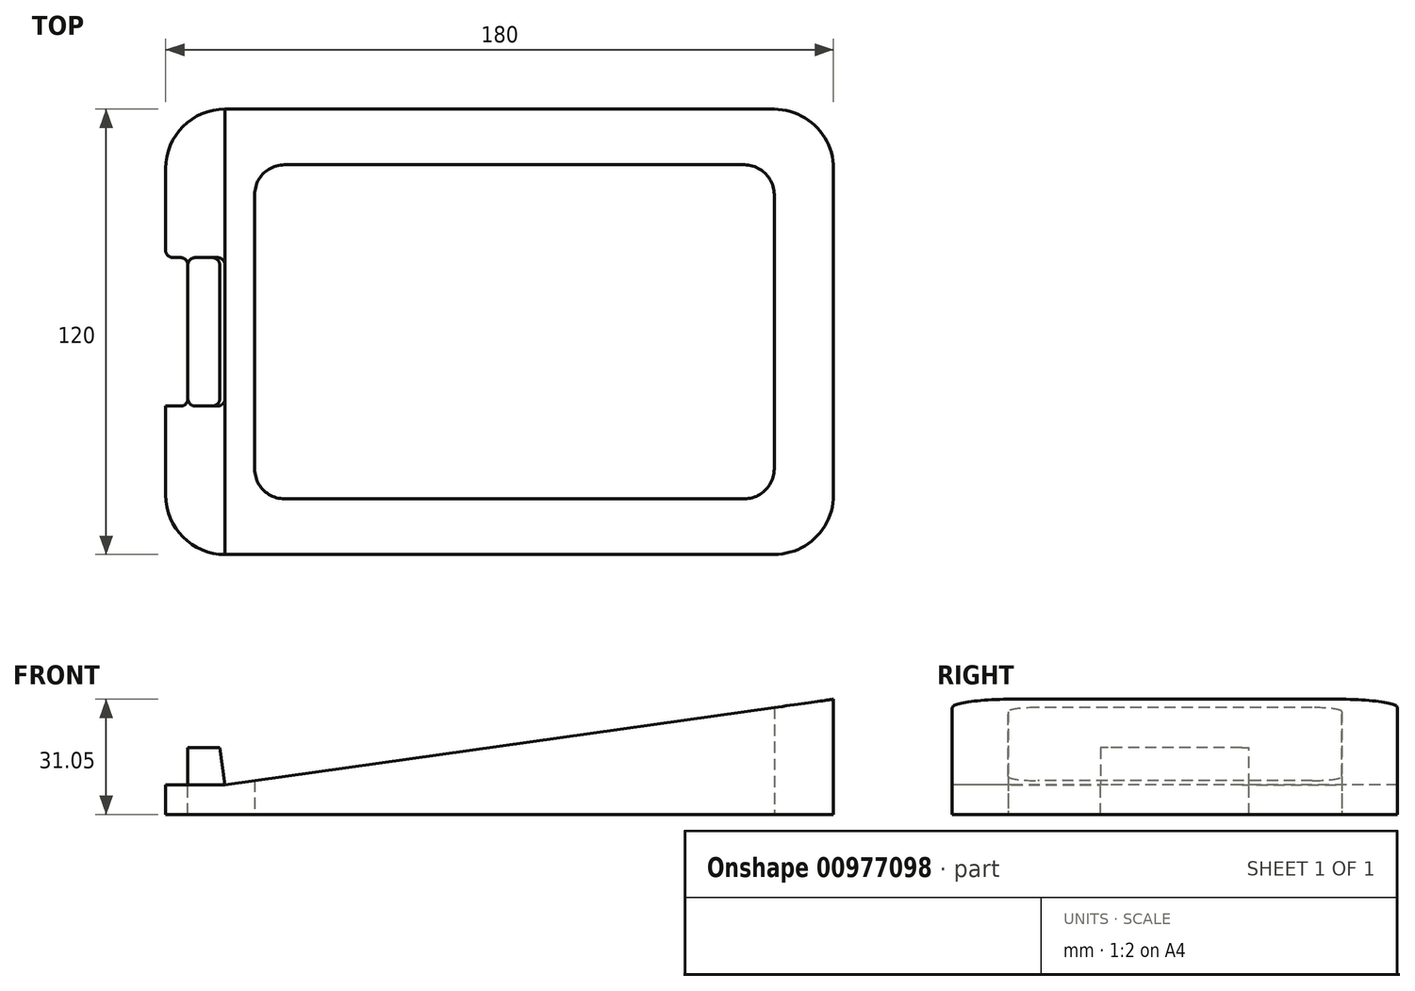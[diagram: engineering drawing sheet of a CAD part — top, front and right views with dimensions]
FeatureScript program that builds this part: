
annotation { "Feature Type Name" : "Feature", "Feature Type Description" : "" }
export const myFeature = defineFeature(function(context is Context, id is Id, definition is map)
    precondition{}
    {
        {
            assignVariable(context, id + "F0", {"name" : "Incline", "anyValue" : 8});
        }
        {
            var Q0;
            Q0=qCreatedBy(makeId("Top.planeOp"),FACE);
            var sketch = newSketch(context, id + "F1", { "sketchPlane" : qUnion([Q0])});
            skLineSegment(sketch, "E0.bottom", {"start": v(0, 0) * mm, "end": v(180, 0) * mm});
            skLineSegment(sketch, "E0.top", {"start": v(0, 120) * mm, "end": v(180, 120) * mm});
            skLineSegment(sketch, "E0.left", {"start": v(0, 0) * mm, "end": v(0, 120) * mm});
            skLineSegment(sketch, "E0.right", {"start": v(180, 0) * mm, "end": v(180, 120) * mm});
            skSolve(sketch);
        }
        {
            var Q0;
            Q0 = qSketchRegion(id + "F1", true);
            extrude(context, id + "F2", {"entities" : qUnion([Q0]), "depth" : 8 * mm, "offsetDistance" : 25 * mm});
        }
        {
            var Q0;
            Q0=makeQuery(id+"F2.opExtrude","SWEPT_FACE",FACE,{"disambiguationData":[OSD([sQuery(id+"F1.wireOp",EDGE,"E0.bottom")])]});
            var sketch = newSketch(context, id + "F3", { "sketchPlane" : qUnion([Q0])});
            skLineSegment(sketch, "E1", {"start": v(180, 8) * mm, "end": v(16, 8) * mm});
            skLineSegment(sketch, "E2", {"start": v(16, 8) * mm, "end": v(180, 31.05) * mm});
            skLineSegment(sketch, "E3", {"start": v(180, 31.05) * mm, "end": v(180, 8) * mm});
            skSolve(sketch);
        }
        {
            var Q0;
            Q0 = qSketchRegion(id + "F3", true);
            extrude(context, id + "F4", {"entities" : qUnion([Q0]), "operationType" : NewBodyOperationType.ADD, "oppositeDirection" : true, "depth" : 120 * mm, "offsetDistance" : 25 * mm});
        }
        {
            var Q0;
            Q0=makeQuery(id+"F2.opExtrude","CAP_FACE",FACE,{"disambiguationData":[OSD([sQuery(id+"F1.wireOp",EDGE,"E0.bottom"),sQuery(id+"F1.wireOp",EDGE,"E0.top"),sQuery(id+"F1.wireOp",EDGE,"E0.left"),sQuery(id+"F1.wireOp",EDGE,"E0.right")])],"isStart":false});
            var sketch = newSketch(context, id + "F5", { "sketchPlane" : qUnion([Q0])});
            skLineSegment(sketch, "E4.bottom", {"start": v(6, 80) * mm, "end": v(16, 80) * mm});
            skLineSegment(sketch, "E4.top", {"start": v(6, 40) * mm, "end": v(16, 40) * mm});
            skLineSegment(sketch, "E4.left", {"start": v(6, 80) * mm, "end": v(6, 40) * mm});
            skLineSegment(sketch, "E4.right", {"start": v(16, 80) * mm, "end": v(16, 40) * mm});
            skLineSegment(sketch, "E5", {"start": v(16, 60) * mm, "end": v(16, 60) * mm});
            skSolve(sketch);
        }
        {
            var Q0;
            Q0 = qSketchRegion(id + "F5", true);
            extrude(context, id + "F6", {"entities" : qUnion([Q0]), "operationType" : NewBodyOperationType.ADD, "depth" : 10 * mm, "offsetDistance" : 25 * mm});
        }
        {
            var Q0;
            Q0=makeQuery(id+"F6.opExtrude","CAP_EDGE",EDGE,{"disambiguationData":[OSD([sQuery(id+"F5.wireOp",EDGE,"E4.right")])],"isStart":false});
            chamfer(context, id + "F7", {"entities" : qUnion([Q0]), "chamferType" : ChamferType.OFFSET_ANGLE, "width" : 10 * mm, "oppositeDirection" : false, "angle" : (getVariable(context, 'Incline')) * degree, "tangentPropagation" : true});
        }
        {
            var Q0;
            Q0=makeQuery(id+"F2.opExtrude","CAP_FACE",FACE,{"disambiguationData":[OSD([sQuery(id+"F1.wireOp",EDGE,"E0.bottom"),sQuery(id+"F1.wireOp",EDGE,"E0.top"),sQuery(id+"F1.wireOp",EDGE,"E0.left"),sQuery(id+"F1.wireOp",EDGE,"E0.right")])],"isStart":true});
            var sketch = newSketch(context, id + "F8", { "sketchPlane" : qUnion([Q0])});
            skLineSegment(sketch, "E6.bottom", {"start": v(164, -15) * mm, "end": v(24, -15) * mm});
            skLineSegment(sketch, "E6.top", {"start": v(164, -105) * mm, "end": v(24, -105) * mm});
            skLineSegment(sketch, "E6.left", {"start": v(164, -15) * mm, "end": v(164, -105) * mm});
            skLineSegment(sketch, "E6.right", {"start": v(24, -15) * mm, "end": v(24, -105) * mm});
            skLineSegment(sketch, "E7", {"start": v(180, -60) * mm, "end": v(164, -60) * mm, "construction": true});
            skSolve(sketch);
        }
        {
            var Q0;
            Q0 = qSketchRegion(id + "F8", true);
            extrude(context, id + "F9", {"entities" : qUnion([Q0]), "operationType" : NewBodyOperationType.REMOVE, "endBound" : BoundingType.UP_TO_NEXT, "oppositeDirection" : true, "depth" : 25 * mm, "offsetDistance" : 25 * mm});
        }
        {
            var Q0;
            Q0=makeQuery(id+"F2.opExtrude","SWEPT_EDGE",EDGE,{"disambiguationData":[OSD([sQuery(id+"F1.wireOp",EDGE,"E0.bottom"),sQuery(id+"F1.wireOp",EDGE,"E0.left")])]});
            var Q1;
            Q1=makeQuery(id+"F2.opExtrude","SWEPT_EDGE",EDGE,{"disambiguationData":[OSD([sQuery(id+"F1.wireOp",EDGE,"E0.top"),sQuery(id+"F1.wireOp",EDGE,"E0.left")])]});
            var Q2;
            Q2=makeQuery(id+"F4.boolean.opBoolean","MERGE",EDGE,{"derivedFrom":[makeQuery(id+"F2.opExtrude","SWEPT_EDGE",EDGE,{"disambiguationData":[OSD([sQuery(id+"F1.wireOp",EDGE,"E0.top"),sQuery(id+"F1.wireOp",EDGE,"E0.right")])]}),makeQuery(id+"F4.opExtrude","CAP_EDGE",EDGE,{"disambiguationData":[OSD([sQuery(id+"F3.wireOp",EDGE,"E3")])],"isStart":false})]});
            var Q3;
            Q3=makeQuery(id+"F4.boolean.opBoolean","MERGE",EDGE,{"derivedFrom":[makeQuery(id+"F2.opExtrude","SWEPT_EDGE",EDGE,{"disambiguationData":[OSD([sQuery(id+"F1.wireOp",EDGE,"E0.bottom"),sQuery(id+"F1.wireOp",EDGE,"E0.right")])]}),makeQuery(id+"F4.opExtrude","CAP_EDGE",EDGE,{"disambiguationData":[OSD([sQuery(id+"F3.wireOp",EDGE,"E3")])],"isStart":true})]});
            fillet(context, id + "F10", {"entities" : qUnion([Q0, Q1, Q2, Q3]), "radius" : 16 * mm, "tangentPropagation" : true, "allowEdgeOverflow" : false});
        }
        {
            var Q0;
            Q0=makeQuery(id+"F9.boolean.opBoolean","COPY",EDGE,{"derivedFrom":makeQuery(id+"F9.opExtrude","SWEPT_EDGE",EDGE,{"disambiguationData":[OSD([sQuery(id+"F8.wireOp",EDGE,"E6.top"),sQuery(id+"F8.wireOp",EDGE,"E6.left")])]})});
            var Q1;
            Q1=makeQuery(id+"F9.boolean.opBoolean","COPY",EDGE,{"derivedFrom":makeQuery(id+"F9.opExtrude","SWEPT_EDGE",EDGE,{"disambiguationData":[OSD([sQuery(id+"F8.wireOp",EDGE,"E6.bottom"),sQuery(id+"F8.wireOp",EDGE,"E6.left")])]})});
            var Q2;
            Q2=makeQuery(id+"F9.boolean.opBoolean","COPY",EDGE,{"derivedFrom":makeQuery(id+"F9.opExtrude","SWEPT_EDGE",EDGE,{"disambiguationData":[OSD([sQuery(id+"F8.wireOp",EDGE,"E6.bottom"),sQuery(id+"F8.wireOp",EDGE,"E6.right")])]})});
            var Q3;
            Q3=makeQuery(id+"F9.boolean.opBoolean","COPY",EDGE,{"derivedFrom":makeQuery(id+"F9.opExtrude","SWEPT_EDGE",EDGE,{"disambiguationData":[OSD([sQuery(id+"F8.wireOp",EDGE,"E6.top"),sQuery(id+"F8.wireOp",EDGE,"E6.right")])]})});
            fillet(context, id + "F11", {"entities" : qUnion([Q0, Q1, Q2, Q3]), "radius" : 8 * mm, "tangentPropagation" : true, "allowEdgeOverflow" : false});
        }
        {
            var Q0;
            Q0=makeQuery(id+"F2.opExtrude","CAP_FACE",FACE,{"disambiguationData":[OSD([sQuery(id+"F1.wireOp",EDGE,"E0.bottom"),sQuery(id+"F1.wireOp",EDGE,"E0.top"),sQuery(id+"F1.wireOp",EDGE,"E0.left"),sQuery(id+"F1.wireOp",EDGE,"E0.right")])],"isStart":false});
            var sketch = newSketch(context, id + "F12", { "sketchPlane" : qUnion([Q0])});
            skLineSegment(sketch, "E8.bottom", {"start": v(6, 80) * mm, "end": v(0, 80) * mm});
            skLineSegment(sketch, "E8.top", {"start": v(6, 40) * mm, "end": v(0, 40) * mm});
            skLineSegment(sketch, "E8.left", {"start": v(6, 80) * mm, "end": v(6, 40) * mm});
            skLineSegment(sketch, "E8.right", {"start": v(0, 80) * mm, "end": v(0, 40) * mm});
            skSolve(sketch);
        }
        {
            var Q0;
            Q0 = qSketchRegion(id + "F12", true);
            extrude(context, id + "F13", {"entities" : qUnion([Q0]), "operationType" : NewBodyOperationType.REMOVE, "endBound" : BoundingType.UP_TO_NEXT, "oppositeDirection" : true, "depth" : 25 * mm, "offsetDistance" : 25 * mm});
        }
        {
            var Q0;
            Q0=makeQuery(id+"F13.boolean.opBoolean","COPY",EDGE,{"derivedFrom":makeQuery(id+"F13.opExtrude","SWEPT_EDGE",EDGE,{"disambiguationData":[OSD([sQuery(id+"F5.wireOp",EDGE,"E4.bottom"),sQuery(id+"F5.wireOp",EDGE,"E4.left"),sQuery(id+"F12.wireOp",EDGE,"E8.bottom"),sQuery(id+"F12.wireOp",EDGE,"E8.left")])]})});
            var Q1;
            Q1=makeQuery(id+"F13.boolean.opBoolean","COPY",EDGE,{"derivedFrom":makeQuery(id+"F13.opExtrude","SWEPT_EDGE",EDGE,{"disambiguationData":[OSD([sQuery(id+"F1.wireOp",EDGE,"E0.left"),sQuery(id+"F12.wireOp",EDGE,"E8.bottom"),sQuery(id+"F12.wireOp",EDGE,"E8.right")])]})});
            var Q2;
            Q2=makeQuery(id+"F13.boolean.opBoolean","COPY",EDGE,{"derivedFrom":makeQuery(id+"F13.opExtrude","SWEPT_EDGE",EDGE,{"disambiguationData":[OSD([sQuery(id+"F5.wireOp",EDGE,"E4.top"),sQuery(id+"F5.wireOp",EDGE,"E4.left"),sQuery(id+"F12.wireOp",EDGE,"E8.top"),sQuery(id+"F12.wireOp",EDGE,"E8.left")])]})});
            var Q3;
            Q3=makeQuery(id+"F13.boolean.opBoolean","COPY",EDGE,{"derivedFrom":makeQuery(id+"F13.opExtrude","SWEPT_EDGE",EDGE,{"disambiguationData":[OSD([sQuery(id+"F1.wireOp",EDGE,"E0.left"),sQuery(id+"F12.wireOp",EDGE,"E8.top"),sQuery(id+"F12.wireOp",EDGE,"E8.right")])]})});
            fillet(context, id + "F14", {"entities" : qUnion([Q0, Q1, Q2, Q3]), "radius" : 2 * mm, "tangentPropagation" : true, "allowEdgeOverflow" : false});
        }
        {
            var Q0;
            Q0=makeQuery(id+"F6.opExtrude","SWEPT_EDGE",EDGE,{"disambiguationData":[OSD([sQuery(id+"F5.wireOp",EDGE,"E4.top"),sQuery(id+"F5.wireOp",EDGE,"E4.left")])]});
            var Q1;
            Q1=makeQuery(id+"F6.opExtrude","SWEPT_EDGE",EDGE,{"disambiguationData":[OSD([sQuery(id+"F5.wireOp",EDGE,"E4.bottom"),sQuery(id+"F5.wireOp",EDGE,"E4.left")])]});
            var Q2;
            Q2=makeQuery(id+"F7.opChamfer","BLEND_EDGE",EDGE,{"blendedFrom":[makeQuery(id+"F6.opExtrude","CAP_EDGE",EDGE,{"disambiguationData":[OSD([sQuery(id+"F5.wireOp",EDGE,"E4.right")])],"isStart":false}),makeQuery(id+"F6.opExtrude","SWEPT_FACE",FACE,{"disambiguationData":[OSD([sQuery(id+"F5.wireOp",EDGE,"E4.top")])]})],"blendedInto":[makeQuery(id+"F6.opExtrude","SWEPT_FACE",FACE,{"disambiguationData":[OSD([sQuery(id+"F5.wireOp",EDGE,"E4.top")])]})]});
            var Q3;
            Q3=makeQuery(id+"F7.opChamfer","BLEND_EDGE",EDGE,{"blendedFrom":[makeQuery(id+"F6.opExtrude","CAP_EDGE",EDGE,{"disambiguationData":[OSD([sQuery(id+"F5.wireOp",EDGE,"E4.right")])],"isStart":false}),makeQuery(id+"F6.opExtrude","SWEPT_FACE",FACE,{"disambiguationData":[OSD([sQuery(id+"F5.wireOp",EDGE,"E4.bottom")])]})],"blendedInto":[makeQuery(id+"F6.opExtrude","SWEPT_FACE",FACE,{"disambiguationData":[OSD([sQuery(id+"F5.wireOp",EDGE,"E4.bottom")])]})]});
            fillet(context, id + "F15", {"entities" : qUnion([Q0, Q1, Q2, Q3]), "radius" : 2 * mm, "tangentPropagation" : true, "allowEdgeOverflow" : false});
        }
    });
